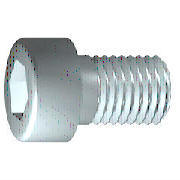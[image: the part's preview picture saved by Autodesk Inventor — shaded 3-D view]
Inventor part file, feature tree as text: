
AUTODESK INVENTOR PART (.ipt)
format: ipt  version: 2017 (Build 210142000, 142)  size: 190,976 bytes
history: native  units: mm (DEFAULTED — no unit token found)
features: sketch x2, other x1, extrude x1, plane x1, fillet x1
ambient origin geometry x7: Origin, YZ Plane, XY Plane, X Axis, Y Axis, Z Axis, Center Point
bodies: Solid1 (feature_tree)
feature tree (6):
  other  "Corps"
  extrude  "Rainure"  Depth=10.75mm
  plane  "Work Plane1"
  fillet  "Fillet2"  Radius=0.306825mm
  sketch  "Esquisse1"
  sketch  "Esquisse2"
